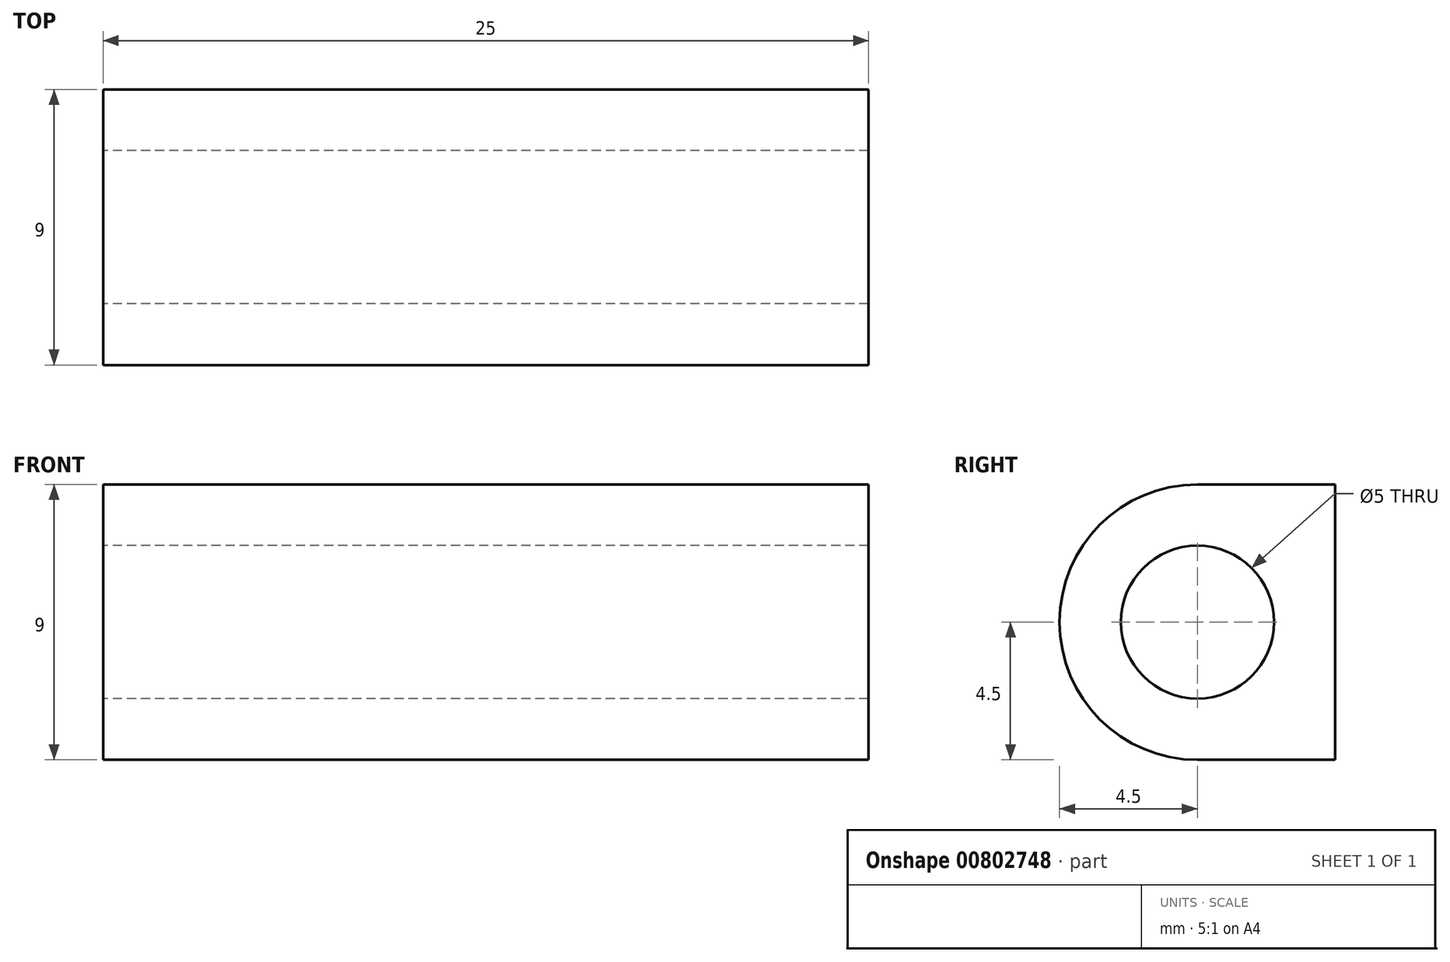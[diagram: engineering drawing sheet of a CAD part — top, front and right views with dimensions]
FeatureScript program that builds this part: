
annotation { "Feature Type Name" : "Feature", "Feature Type Description" : "" }
export const myFeature = defineFeature(function(context is Context, id is Id, definition is map)
    precondition{}
    {
        {
            var Q0;
            Q0=qCreatedBy(makeId("Right.planeOp"),FACE);
            var sketch = newSketch(context, id + "F0", { "sketchPlane" : qUnion([Q0])});
            skArc(sketch, "E0", {"start": v(0, 4.5) * mm, "mid": v(-4.5, 0) * mm, "end": v(0, -4.5) * mm});
            skLineSegment(sketch, "E1.bottom", {"start": v(0, 4.5) * mm, "end": v(4.5, 4.5) * mm});
            skLineSegment(sketch, "E1.top", {"start": v(0, -4.5) * mm, "end": v(4.5, -4.5) * mm});
            skLineSegment(sketch, "E1.right", {"start": v(4.5, 4.5) * mm, "end": v(4.5, -4.5) * mm});
            skCircle(sketch, "E2", {"center": v(0, 0) * mm, "radius": 2.5 * mm});
            skSolve(sketch);
        }
        {
            var Q0;
            Q0=makeQuery(id+"F0.imprint","IMPRINT",FACE,{"disambiguationData":[TD([[makeQuery(id+"F0.imprint","IMPRINT",EDGE,{"derivedFrom":sQuery(id+"F0.wireOp",EDGE,"E0")}),1.0]])]});
            extrude(context, id + "F1", {"entities" : qUnion([Q0]), "depth" : 25 * mm, "offsetDistance" : 25 * mm});
        }
    });
